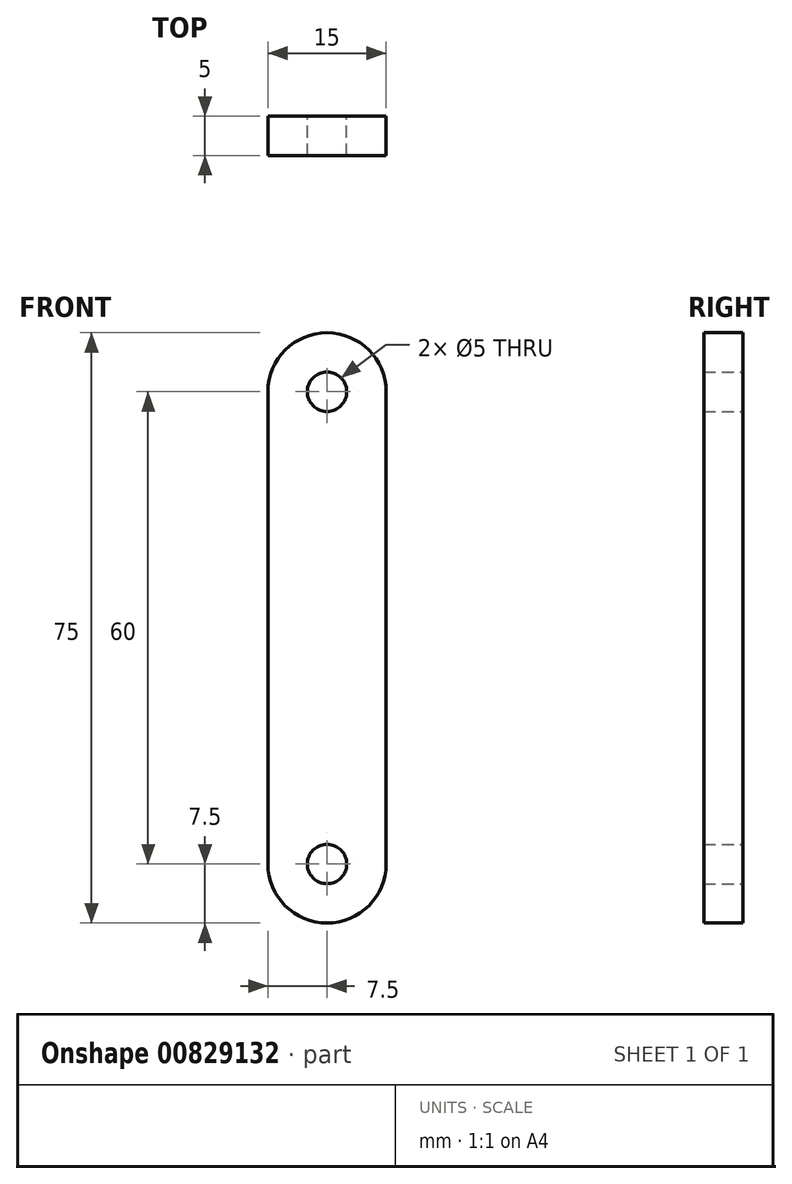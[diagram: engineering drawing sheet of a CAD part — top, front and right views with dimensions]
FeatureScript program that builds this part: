
annotation { "Feature Type Name" : "Feature", "Feature Type Description" : "" }
export const myFeature = defineFeature(function(context is Context, id is Id, definition is map)
    precondition{}
    {
        {
            var Q0;
            Q0=qCreatedBy(makeId("Front.planeOp"),FACE);
            var sketch = newSketch(context, id + "F0", { "sketchPlane" : qUnion([Q0])});
            skLineSegment(sketch, "E0.bottom", {"start": v(7.5, 30) * mm, "end": v(-7.5, 30) * mm});
            skLineSegment(sketch, "E0.top", {"start": v(7.5, -30) * mm, "end": v(-7.5, -30) * mm});
            skLineSegment(sketch, "E0.left", {"start": v(7.5, 30) * mm, "end": v(7.5, -30) * mm});
            skLineSegment(sketch, "E0.right", {"start": v(-7.5, 30) * mm, "end": v(-7.5, -30) * mm});
            skPoint(sketch, "E0.middle", {"position": v(0, 0) * mm});
            skArc(sketch, "E1", {"start": v(7.5, 30) * mm, "mid": v(0, 37.5) * mm, "end": v(-7.5, 30) * mm});
            skArc(sketch, "E2", {"start": v(-7.5, -30) * mm, "mid": v(0, -37.5) * mm, "end": v(7.5, -30) * mm});
            skCircle(sketch, "E3", {"center": v(0, 30) * mm, "radius": 2.5 * mm});
            skCircle(sketch, "E4", {"center": v(0, -30) * mm, "radius": 2.5 * mm});
            skSolve(sketch);
        }
        {
            var Q0;
            Q0 = qSketchRegion(id + "F0", true);
            extrude(context, id + "F1", {"entities" : qUnion([Q0]), "depth" : 5 * mm, "offsetDistance" : 25 * mm});
        }
    });
